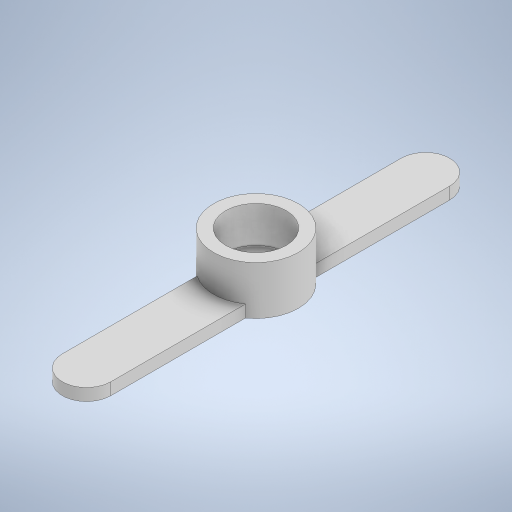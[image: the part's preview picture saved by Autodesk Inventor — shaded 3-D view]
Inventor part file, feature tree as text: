
AUTODESK INVENTOR PART (.ipt)
format: ipt  version: 2024.2 (Build 282272000, 272)  size: 291,328 bytes
history: native  units: mm
features: extrude x5, sketch x5, projected_geometry x3, fillet x1
ambient origin geometry x8: Origin, YZ Plane, XZ Plane, XY Plane, X Axis, Y Axis, Z Axis, Center Point
bodies: Solid1 (feature_tree)
feature tree (14):
  extrude  "Extrusion1"  Depth=1.0mm
  fillet  "Fillet1"  Radius=1.0mm
  extrude  "Extrusion2"  Depth=2.0mm
  extrude  "Extrusion3"  Depth=2.0mm
  extrude  "Extrusion4"  Depth=1.0mm TaperAngle=0.0deg
  extrude  "Extrusion5"  TaperAngle=0.0deg  [1 undecoded]
  sketch  "Sketch1"  dims[d0=4.0mm d1=32.0mm d2=1.0mm d3=0.0mm]
  sketch  "Sketch2"  dims[d4=2.0mm d5=7.0mm]
  sketch  "Sketch3"  dims[d6=16.0mm d7=2.0mm]
  projected_geometry  "Projected Loop1"
  projected_geometry  "Projected Loop2"
  sketch  "Sketch4"  dims[d8=3.0mm d9=0.0mm d10=1.0mm d11=0.0mm]
  projected_geometry  "Projected Loop3"
  sketch  "Sketch5"  dims[d12=2.0mm d13=0.0mm d14=0.0mm d15=5.0mm d16=3.0mm d17=0.0mm]
note: 1 required parameter value undecoded (feature->parameter linkage not recoverable at this tier; creation-order binding heuristic only, values carry confidence <= 0.55)
